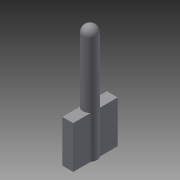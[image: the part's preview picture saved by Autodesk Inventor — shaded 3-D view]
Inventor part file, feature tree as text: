
AUTODESK INVENTOR PART (.ipt)
format: ipt  version: 2015 (Build 190159000, 159)  size: 91,648 bytes
history: native  units: in
note: dims shown in document units (in); Inventor stores cm internally (conversion verified against a paired STEP export)
features: extrude x2, sketch x1, fillet x1
ambient origin geometry x8: Origin, YZ Plane, XZ Plane, XY Plane, X Axis, Y Axis, Z Axis, Center Point
bodies: Solid1 (feature_tree)
feature tree (4):
  sketch  "Sketch1"  dims[d0=0.78in d1=0.19in d2=0.25in d3=0.39in d4=0.095in d5=0.74in d6=0.0in d7=2.0in d8=0.0in d9=0.125in]
  extrude  "Extrusion1"  Depth=0.19in
  extrude  "Extrusion2"  Depth=0.125in
  fillet  "Fillet1"  Radius=0.095in
